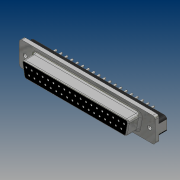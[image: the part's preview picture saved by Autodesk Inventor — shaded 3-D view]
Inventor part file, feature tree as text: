
AUTODESK INVENTOR PART (.ipt)
format: ipt  version: 2012 (Build 160160000, 160)  size: 244,224 bytes
history: native  units: mm (DEFAULTED — no unit token found)
features: sketch x6, extrude x5, projected_geometry x3, hole x1, pattern_linear x1, fillet x1
ambient origin geometry x8: Origin, YZ Plane, XZ Plane, XY Plane, X Axis, Y Axis, Z Axis, Center Point
bodies: Solid1 (feature_tree)
feature tree (17):
  extrude  "Base Flange"  Depth=12.55mm
  extrude  "Socket Side Boss Housing"  Depth=1.27mm
  extrude  "Board Side Plastic Boss"  Depth=54.84mm
  hole  "Hole1"  [1 undecoded]
  extrude  "Pin Extrusion"  Depth=7.1mm
  extrude  "Socket Cut"  Depth=4.08mm TaperAngle=0.0deg
  pattern_linear  "Pin and Hole Pattern"  Spacing1=2.84mm  [1 undecoded]
  fillet  "Fillets"  Radius=0.889mm
  sketch  "Sketch1"  dims[d0=69.39mm d1=12.55mm]
  sketch  "Sketch2"  dims[d4=1.91mm d5=0.0mm d6=1.27mm]
  sketch  "Sketch3"  dims[d7=7.9mm d8=54.84mm]
  sketch  "Sketch5"  dims[d9=1.745329mm d10=1.27mm]
  sketch  "Sketch6"  dims[d11=6.17mm d12=0.0mm d13=7.1mm]
  projected_geometry  "Projected Loop1"
  projected_geometry  "Projected Loop2"
  projected_geometry  "Projected Loop3"
  sketch  "Sketch7"  dims[d15=1.27mm d16=4.08mm d17=0.0mm d23=2.84mm d25=0.889mm d26=2.77mm d27=1.385mm d28=1.42mm d29=24.93mm d30=3.18mm d31=0.0mm d32=6.1mm d33=0.0mm d34=180.0mm d36=2.77mm d37=1.0mm d38=0.5mm d39=63.5mm d40=2.156mm d41=6.0mm d42=4.0mm d43=2.0mm d44=90.0deg d45=8.0mm d46=20.594885mm]
note: 2 required parameter values undecoded (feature->parameter linkage not recoverable at this tier; creation-order binding heuristic only, values carry confidence <= 0.55)
